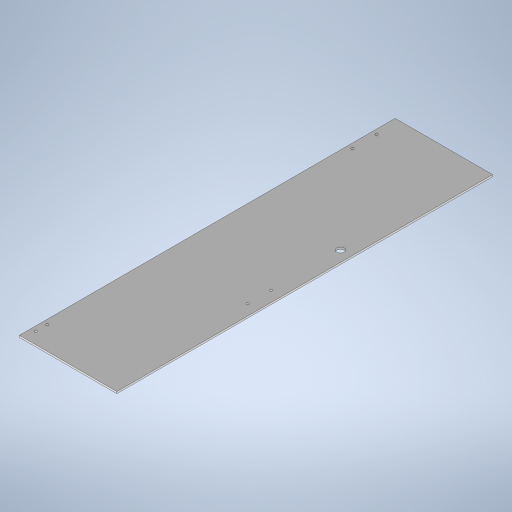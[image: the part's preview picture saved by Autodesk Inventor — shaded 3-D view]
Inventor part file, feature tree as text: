
AUTODESK INVENTOR PART (.ipt)
format: ipt  version: 2023 (Build 270158000, 158)  size: 243,200 bytes
history: native  units: mm
features: other x1, extrude x1, sketch x1
ambient origin geometry x8: Origin, YZ Plane, XZ Plane, XY Plane, X Axis, Y Axis, Z Axis, Center Point
bodies: Body1 (feature_tree)
feature tree (3):
  other  "Твердое тело1"
  extrude  "Выдавливание1"  Depth=210.0mm
  sketch  "Эскиз1"
